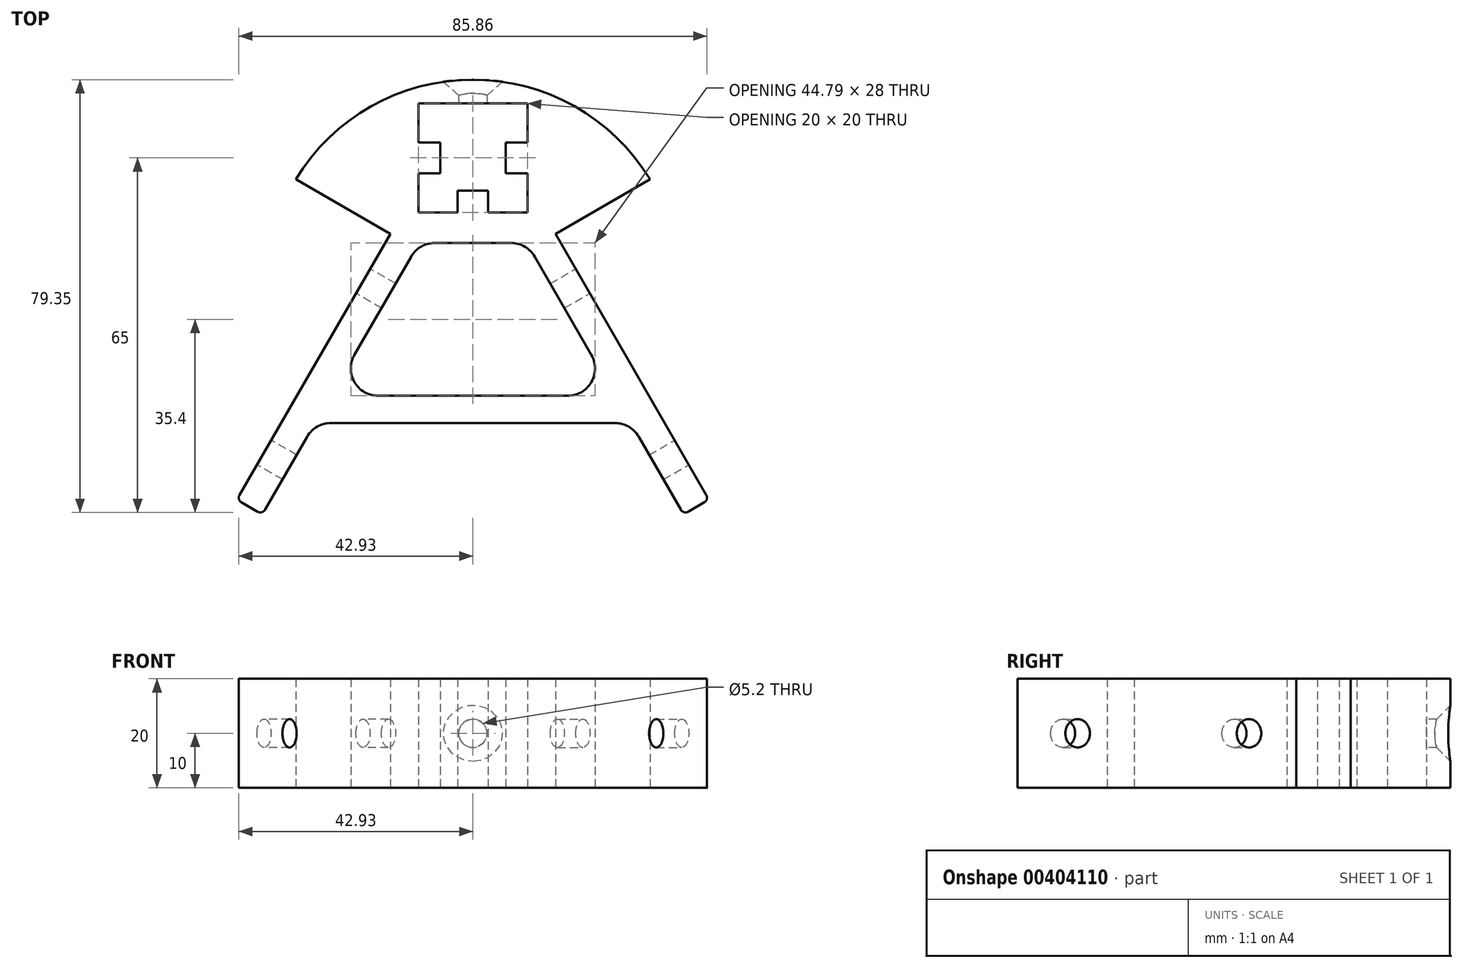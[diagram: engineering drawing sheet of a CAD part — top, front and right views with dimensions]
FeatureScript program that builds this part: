
annotation { "Feature Type Name" : "Feature", "Feature Type Description" : "" }
export const myFeature = defineFeature(function(context is Context, id is Id, definition is map)
    precondition{}
    {
        {
            var Q0;
            Q0=qCreatedBy(makeId("Top.planeOp"),FACE);
            var sketch = newSketch(context, id + "F0", { "sketchPlane" : qUnion([Q0])});
            skLineSegment(sketch, "E0", {"start": v(83.87, -69.28) * mm, "end": v(-83.87, -69.28) * mm, "construction": true});
            skArc(sketch, "E1", {"start": v(32.48, 19.73) * mm, "mid": v(0, 38) * mm, "end": v(-32.47, 19.73) * mm});
            skLineSegment(sketch, "E2", {"start": v(-32.47, 19.73) * mm, "end": v(-15.15, 9.73) * mm});
            skLineSegment(sketch, "E3", {"start": v(32.48, 19.73) * mm, "end": v(15.15, 9.73) * mm});
            skLineSegment(sketch, "E4", {"start": v(-15.15, 9.73) * mm, "end": v(-42.8, -38.15) * mm});
            skLineSegment(sketch, "E5", {"start": v(-42.43, -39.52) * mm, "end": v(-39.49, -41.22) * mm});
            skLineSegment(sketch, "E6", {"start": v(-38.12, -40.85) * mm, "end": v(-30.39, -27.45) * mm});
            skLineSegment(sketch, "E7", {"start": v(-26.06, -24.95) * mm, "end": v(26.06, -24.95) * mm});
            skLineSegment(sketch, "E8", {"start": v(30.39, -27.45) * mm, "end": v(38.12, -40.85) * mm});
            skLineSegment(sketch, "E9", {"start": v(39.49, -41.22) * mm, "end": v(42.43, -39.52) * mm});
            skLineSegment(sketch, "E10", {"start": v(42.8, -38.15) * mm, "end": v(15.15, 9.73) * mm});
            skLineSegment(sketch, "E11", {"start": v(0, 75.98) * mm, "end": v(-83.87, -69.28) * mm, "construction": true});
            skLineSegment(sketch, "E12", {"start": v(0, 75.98) * mm, "end": v(83.87, -69.28) * mm, "construction": true});
            skLineSegment(sketch, "E13", {"start": v(-7, 8.05) * mm, "end": v(7, 8.05) * mm});
            skLineSegment(sketch, "E14", {"start": v(11.33, 5.55) * mm, "end": v(21.73, -12.45) * mm});
            skLineSegment(sketch, "E15", {"start": v(17.4, -19.95) * mm, "end": v(-17.4, -19.95) * mm});
            skLineSegment(sketch, "E16", {"start": v(-21.73, -12.45) * mm, "end": v(-11.33, 5.55) * mm});
            skLineSegment(sketch, "E17", {"start": v(28.94, -24.95) * mm, "end": v(26.06, -19.95) * mm, "construction": true});
            skLineSegment(sketch, "E18", {"start": v(-28.94, -24.95) * mm, "end": v(-26.06, -19.95) * mm, "construction": true});
            skPoint(sketch, "E19", {"position": v(0, -24.95) * mm});
            skLineSegment(sketch, "E20.bottom", {"start": v(-10, 33.65) * mm, "end": v(10, 33.65) * mm, "construction": true});
            skLineSegment(sketch, "E20.top", {"start": v(-10, 13.65) * mm, "end": v(10, 13.65) * mm, "construction": true});
            skLineSegment(sketch, "E20.left", {"start": v(-10, 33.65) * mm, "end": v(-10, 13.65) * mm, "construction": true});
            skLineSegment(sketch, "E20.right", {"start": v(10, 33.65) * mm, "end": v(10, 13.65) * mm, "construction": true});
            skPoint(sketch, "E21", {"position": v(0, 33.65) * mm});
            skPoint(sketch, "E22", {"position": v(-38.3, -30.36) * mm});
            skPoint(sketch, "E23", {"position": v(-20.15, 1.07) * mm});
            skLineSegment(sketch, "E24", {"start": v(-10, 13.65) * mm, "end": v(-10, 20.85) * mm});
            skLineSegment(sketch, "E25", {"start": v(-10, 20.85) * mm, "end": v(-6, 20.85) * mm});
            skLineSegment(sketch, "E26", {"start": v(-6, 20.85) * mm, "end": v(-6, 26.45) * mm});
            skLineSegment(sketch, "E27", {"start": v(-6, 26.45) * mm, "end": v(-10, 26.45) * mm});
            skPoint(sketch, "E27.endSnap0", {"position": v(-10, 23.65) * mm});
            skLineSegment(sketch, "E28", {"start": v(-10, 26.45) * mm, "end": v(-10, 33.65) * mm});
            skLineSegment(sketch, "E29", {"start": v(-10, 13.65) * mm, "end": v(-2.8, 13.65) * mm});
            skLineSegment(sketch, "E30", {"start": v(-2.8, 13.65) * mm, "end": v(-2.8, 17.65) * mm});
            skLineSegment(sketch, "E31", {"start": v(-2.8, 17.65) * mm, "end": v(2.8, 17.65) * mm});
            skLineSegment(sketch, "E32", {"start": v(2.8, 17.65) * mm, "end": v(2.8, 13.65) * mm});
            skLineSegment(sketch, "E33", {"start": v(2.8, 13.65) * mm, "end": v(10, 13.65) * mm});
            skLineSegment(sketch, "E34", {"start": v(10, 13.65) * mm, "end": v(10, 20.85) * mm});
            skLineSegment(sketch, "E35", {"start": v(10, 20.85) * mm, "end": v(6, 20.85) * mm});
            skLineSegment(sketch, "E36", {"start": v(6, 20.85) * mm, "end": v(6, 26.45) * mm});
            skLineSegment(sketch, "E37", {"start": v(6, 26.45) * mm, "end": v(10, 26.45) * mm});
            skLineSegment(sketch, "E38", {"start": v(10, 26.45) * mm, "end": v(10, 33.65) * mm});
            skLineSegment(sketch, "E39", {"start": v(10, 33.65) * mm, "end": v(-10, 33.65) * mm});
            skPoint(sketch, "E40.visualSharp", {"position": v(-26.06, -19.95) * mm});
            skArc(sketch, "E40.filletArc", {"start": v(-21.73, -12.45) * mm, "mid": v(-21.73, -17.45) * mm, "end": v(-17.4, -19.95) * mm});
            skPoint(sketch, "E41.visualSharp", {"position": v(-28.94, -24.95) * mm});
            skArc(sketch, "E41.filletArc", {"start": v(-26.06, -24.95) * mm, "mid": v(-28.56, -25.62) * mm, "end": v(-30.39, -27.45) * mm});
            skPoint(sketch, "E42.visualSharp", {"position": v(28.94, -24.95) * mm});
            skArc(sketch, "E42.filletArc", {"start": v(30.39, -27.45) * mm, "mid": v(28.56, -25.62) * mm, "end": v(26.06, -24.95) * mm});
            skPoint(sketch, "E43.visualSharp", {"position": v(26.06, -19.95) * mm});
            skArc(sketch, "E43.filletArc", {"start": v(17.4, -19.95) * mm, "mid": v(21.73, -17.45) * mm, "end": v(21.73, -12.45) * mm});
            skPoint(sketch, "E44.visualSharp", {"position": v(-9.9, 8.05) * mm});
            skArc(sketch, "E44.filletArc", {"start": v(-7, 8.05) * mm, "mid": v(-9.5, 7.38) * mm, "end": v(-11.33, 5.55) * mm});
            skPoint(sketch, "E45.visualSharp", {"position": v(9.9, 8.05) * mm});
            skArc(sketch, "E45.filletArc", {"start": v(11.33, 5.55) * mm, "mid": v(9.5, 7.38) * mm, "end": v(7, 8.05) * mm});
            skPoint(sketch, "E46.visualSharp", {"position": v(-38.62, -41.72) * mm});
            skArc(sketch, "E46.filletArc", {"start": v(-39.49, -41.22) * mm, "mid": v(-38.73, -41.32) * mm, "end": v(-38.12, -40.85) * mm});
            skPoint(sketch, "E47.visualSharp", {"position": v(-43.3, -39.02) * mm});
            skArc(sketch, "E47.filletArc", {"start": v(-42.8, -38.15) * mm, "mid": v(-42.9, -38.9) * mm, "end": v(-42.43, -39.52) * mm});
            skPoint(sketch, "E48.visualSharp", {"position": v(38.62, -41.72) * mm});
            skArc(sketch, "E48.filletArc", {"start": v(38.12, -40.85) * mm, "mid": v(38.73, -41.32) * mm, "end": v(39.49, -41.22) * mm});
            skPoint(sketch, "E49.visualSharp", {"position": v(43.3, -39.02) * mm});
            skArc(sketch, "E49.filletArc", {"start": v(42.43, -39.52) * mm, "mid": v(42.9, -38.9) * mm, "end": v(42.8, -38.15) * mm});
            skSolve(sketch);
        }
        {
            var Q0;
            Q0=qSketchRegion(id+"F0",true);
            extrude(context, id + "F1", {"entities" : qUnion([Q0]), "depth" : 20 * mm});
        }
        {
            var Q0;
            Q0=makeQuery(id+"F1.opExtrude","SWEPT_FACE",FACE,{"disambiguationData":[OSD([sQuery(id+"F0.wireOp",EDGE,"E4")])]});
            var sketch = newSketch(context, id + "F2", { "sketchPlane" : qUnion([Q0])});
            skCircle(sketch, "E50", {"center": v(45.44, 10) * mm, "radius": 2.6 * mm});
            skCircle(sketch, "E51", {"center": v(9.15, 10) * mm, "radius": 2.6 * mm});
            skLineSegment(sketch, "E52", {"start": v(-0.85, 10) * mm, "end": v(55.44, 10) * mm, "construction": true});
            skSolve(sketch);
        }
        {
            var Q0;
            Q0=qSketchRegion(id+"F2",true);
            extrude(context, id + "F3", {"entities" : qUnion([Q0]), "operationType" : NewBodyOperationType.REMOVE, "oppositeDirection" : true, "depth" : 10 * mm});
        }
        {
            var Q0;
            Q0=makeQuery(id+"F1.opExtrude","SWEPT_FACE",FACE,{"disambiguationData":[OSD([sQuery(id+"F0.wireOp",EDGE,"E10")])]});
            var sketch = newSketch(context, id + "F4", { "sketchPlane" : qUnion([Q0])});
            skLineSegment(sketch, "E53", {"start": v(0.85, 10) * mm, "end": v(-55.44, 10) * mm, "construction": true});
            skCircle(sketch, "E54", {"center": v(-9.15, 10) * mm, "radius": 2.6 * mm});
            skCircle(sketch, "E55", {"center": v(-45.44, 10) * mm, "radius": 2.6 * mm});
            skSolve(sketch);
        }
        {
            var Q0;
            Q0=qSketchRegion(id+"F4",true);
            extrude(context, id + "F5", {"entities" : qUnion([Q0]), "operationType" : NewBodyOperationType.REMOVE, "oppositeDirection" : true, "depth" : 10 * mm});
        }
        {
            var Q0;
            Q0=makeQuery(id+"F1.opExtrude","SWEPT_FACE",FACE,{"disambiguationData":[OSD([sQuery(id+"F0.wireOp",EDGE,"E39")])]});
            var sketch = newSketch(context, id + "F6", { "sketchPlane" : qUnion([Q0])});
            skCircle(sketch, "E56", {"center": v(0, 10) * mm, "radius": 2.6 * mm});
            skSolve(sketch);
        }
        {
            var Q0;
            Q0=qSketchRegion(id+"F6",true);
            extrude(context, id + "F7", {"entities" : qUnion([Q0]), "operationType" : NewBodyOperationType.REMOVE, "oppositeDirection" : true, "depth" : 25 * mm});
        }
        {
            var Q0;
            Q0=makeQuery(id+"F7.boolean.opBoolean","INTERSECT",EDGE,{"derivedFrom":[makeQuery(id+"F1.opExtrude","SWEPT_FACE",FACE,{"disambiguationData":[OSD([sQuery(id+"F0.wireOp",EDGE,"E1")])]}),makeQuery(id+"F7.opExtrude","SWEPT_FACE",FACE,{"disambiguationData":[OSD([sQuery(id+"F6.wireOp",EDGE,"E56")])]})]});
            chamfer(context, id + "F8", {"entities" : qUnion([Q0]), "width" : 2.5 * mm, "tangentPropagation" : true});
        }
    });
